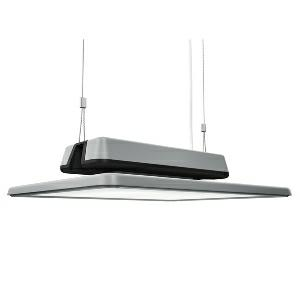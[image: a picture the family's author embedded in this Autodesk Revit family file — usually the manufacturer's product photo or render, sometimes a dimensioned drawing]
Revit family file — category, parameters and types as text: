
# Revit family: acaneo_-_hial_37000_840_w_dali_00804839_445c
name_source: partatom
category: Lighting Fixtures
units: mm (PartAtom-declared; Revit-internal decimal feet)

## family parameters
Cut with Voids When Loaded = No
Host = Face
Light Source = No
Part Type = Normal
Room Calculation Point = No
Round Connector Dimension = Use Diameter
Shared = No

## types (1)
- ACANEO - HIAL 37000/840/W/DALI (1 x LED, 40000 lm, 4000K)
    Apparent Load = 262 VA
    Approval mark = CE
    CIE Flux Codes = 76 97 99 100 100
    Color Rendering = 80-89
    Color Temperature = 4000K
    Control Gear = Electronic ballast
    Default Elevation = 1800 mm
    Description = HIAL 37000/840/W/DALI|High bay luminaire|light source: LED|work equipment: Adjustable electronic ballast, digital DALI|connected load: 220-240 V, 50/60 Hz|Power consumption: approx. 262 W|power factor: approx. 0,981|luminous flux: 40000 lm|luminous efficacy: 152 lm/W|colour temperature: Cold white, ca. 4000 K|color rendering index (CRI): >= 80|chromaticity tolerance:  3 SDCM|System of protection: IP 65|class of protection: I|technology: Continuously dimmable|luminaire body|material: Aluminium|surface: Powder coatet|colour: White aluminium|lamp cover: Acrylic (PMMA), Clear|weight (net): approx. 10.8 kg|mains lead: Built-in plug RST 20i5 Einbau|Fastening: Available separately|Accessory: Junction box (RST 20i5)|minimum ambient temperature: -30 ░C|maximum ambient temperature: 50 ░C|glare control: Optics|unified glare rating(4H 8H): <=  25|
    Frequency = 50 Hz, 60 Hz
    Height = 125 mm
    Lamp = 1 x LED
    Lamp Light Flux = 40000 lm
    Lamp count = 1
    Length = 585 mm
    Luminous efficacy = 153 lm/W
    Manufacturer = Waldmann
    ModVariant = No
    Model = 00804839
    Mounting Place = Ceiling
    Mounting Type = Pendant
    Number of Poles = 1
    OnlyDefault = Yes
    Power Factor = 1
    Product Name = ACANEO - HIAL 37000/840/W/DALI
    Product group = High bay luminaire (industry)
    ProductGroupID = 901
    Protection Class = Protection class I
    Protection Degree = IP 65
    RLX_Detail_Level = 1
    RLX_Emergency_Light_Flux = 0 lm
    RLX_Emergency_Type = 0
    RLX_Emergency_Type_DB = No
    RlxData = <blob elided: 29897 chars, md5=2c08d693>
    Socket = socket
    Standby Power = 0 W
    System Light Flux = 40000 lm
    System Power = 262 W
    Type Comments = Product without accessories
    Type Image = acaneo-hial.jpg
    URL = http://relux.com
    VarID = ---
    Voltage = 230 V
    Voltage Range = 110-120 V, 220-240 V
    Weight = 0.00 kg
    Width = 480 mm

## geometry (parser evidence)
native form markers: Blend x4, Sweep x8
no freeform markers — native parametric forms only
